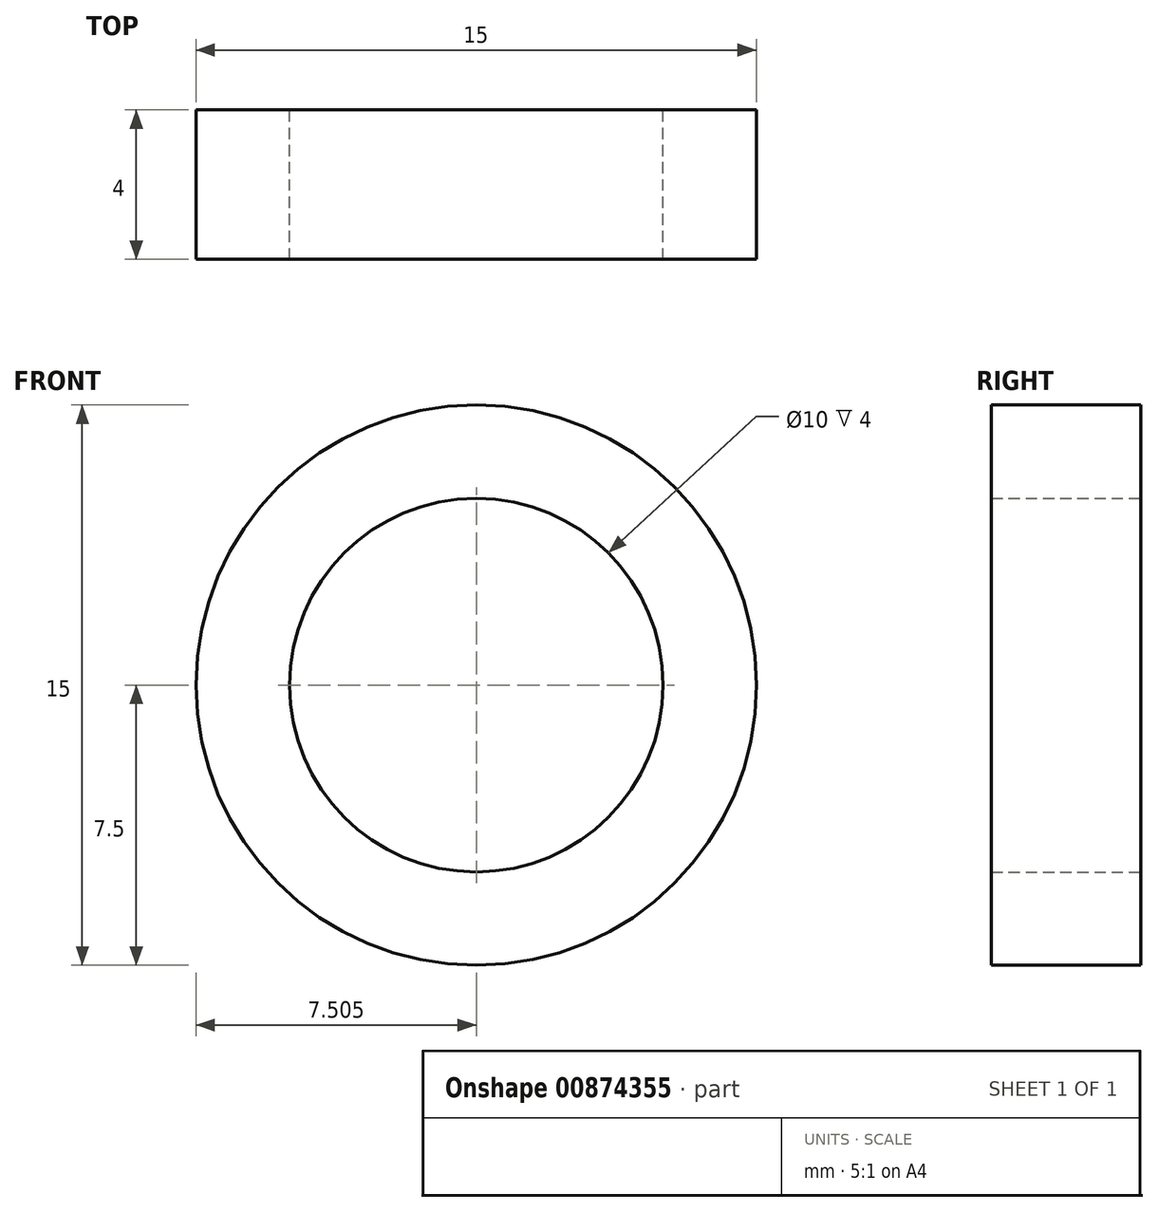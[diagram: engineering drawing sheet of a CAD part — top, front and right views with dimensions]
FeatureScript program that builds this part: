
annotation { "Feature Type Name" : "Feature", "Feature Type Description" : "" }
export const myFeature = defineFeature(function(context is Context, id is Id, definition is map)
    precondition{}
    {
        {
            var Q0;
            Q0=qCreatedBy(makeId("Front.planeOp"),FACE);
            var sketch = newSketch(context, id + "F0", { "sketchPlane" : qUnion([Q0])});
            skCircle(sketch, "E0", {"center": v(-40.03, 33) * mm, "radius": 7.5 * mm});
            skCircle(sketch, "E1", {"center": v(-40.03, 33) * mm, "radius": 5 * mm});
            skSolve(sketch);
        }
        {
            var Q0;
            Q0 = qSketchRegion(id + "F0", true);
            extrude(context, id + "F1", {"entities" : qUnion([Q0]), "depth" : 4 * mm, "offsetDistance" : 25.4 * mm});
        }
    });
